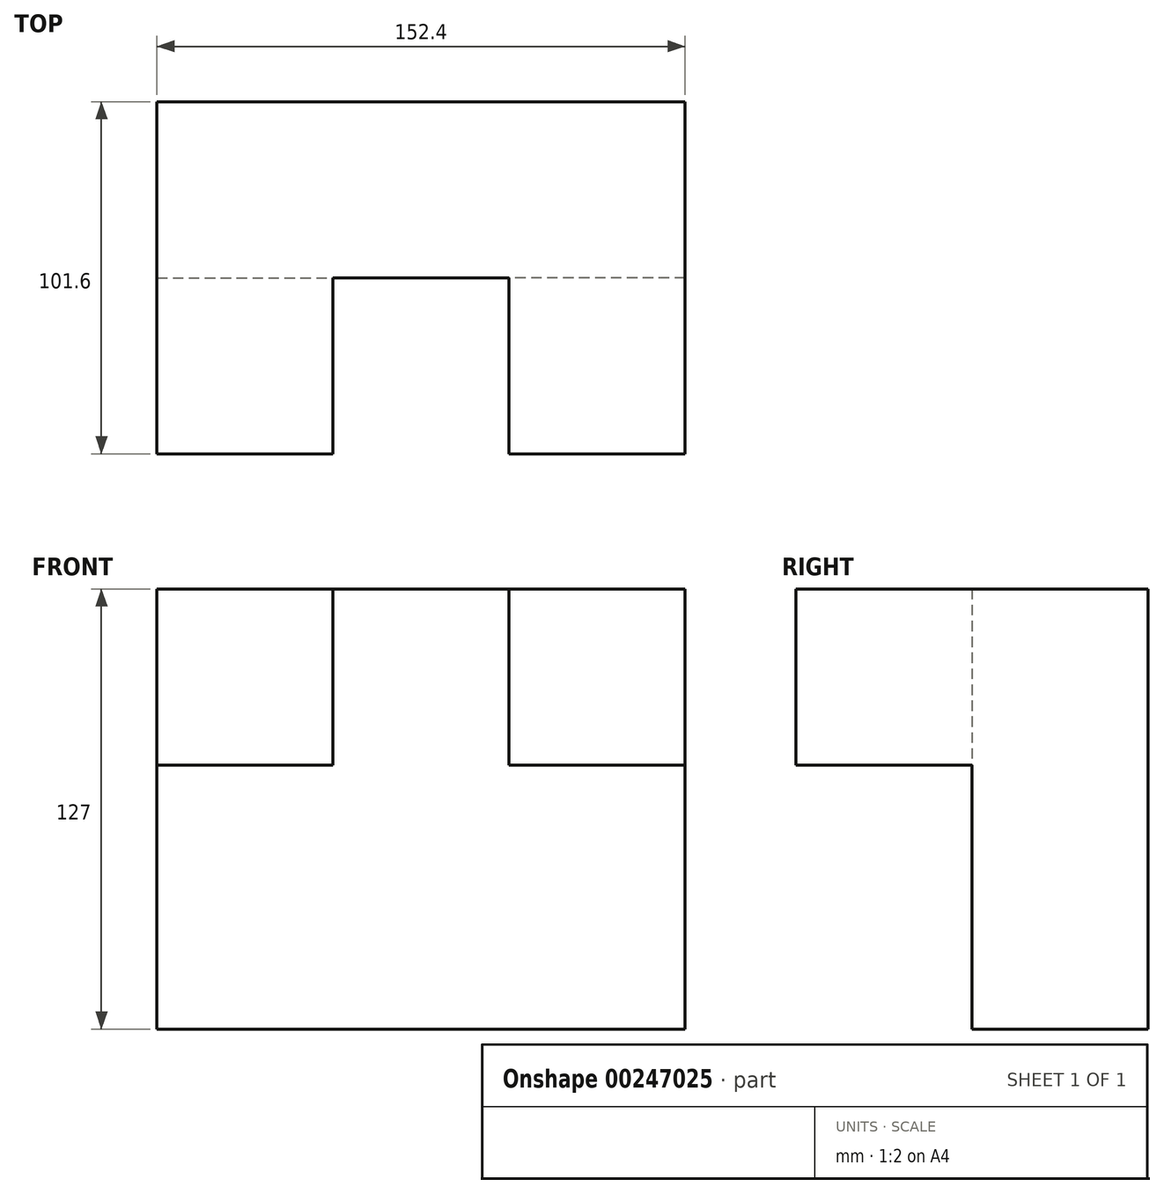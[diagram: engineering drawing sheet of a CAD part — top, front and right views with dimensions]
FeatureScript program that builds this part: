
annotation { "Feature Type Name" : "Feature", "Feature Type Description" : "" }
export const myFeature = defineFeature(function(context is Context, id is Id, definition is map)
    precondition{}
    {
        {
            var Q0;
            Q0=qCreatedBy(makeId("Front.planeOp"),FACE);
            var sketch = newSketch(context, id + "F0", { "sketchPlane" : qUnion([Q0])});
            skLineSegment(sketch, "E0.bottom", {"start": v(-68.04, 132.68) * mm, "end": v(84.36, 132.68) * mm});
            skLineSegment(sketch, "E0.top", {"start": v(-68.04, 5.68) * mm, "end": v(84.36, 5.68) * mm});
            skLineSegment(sketch, "E0.left", {"start": v(-68.04, 132.68) * mm, "end": v(-68.04, 5.68) * mm});
            skLineSegment(sketch, "E0.right", {"start": v(84.36, 132.68) * mm, "end": v(84.36, 5.68) * mm});
            skSolve(sketch);
        }
        {
            var Q0;
            Q0=makeQuery(id+"F0.imprint","IMPRINT",FACE,{"disambiguationData":[TD([[makeQuery(id+"F0.imprint","IMPRINT",EDGE,{"derivedFrom":sQuery(id+"F0.wireOp",EDGE,"E0.bottom")}),-1.0]])]});
            extrude(context, id + "F1", {"entities" : qUnion([Q0]), "depth" : 50.8 * mm});
        }
        {
            var Q0;
            Q0=makeQuery(id+"F1.opExtrude","CAP_FACE",FACE,{"disambiguationData":[OSD([sQuery(id+"F0.wireOp",EDGE,"E0.bottom"),sQuery(id+"F0.wireOp",EDGE,"E0.top"),sQuery(id+"F0.wireOp",EDGE,"E0.left"),sQuery(id+"F0.wireOp",EDGE,"E0.right")])],"isStart":false});
            var sketch = newSketch(context, id + "F2", { "sketchPlane" : qUnion([Q0])});
            skLineSegment(sketch, "E1.bottom", {"start": v(-68.04, 132.68) * mm, "end": v(-17.24, 132.68) * mm});
            skLineSegment(sketch, "E1.top", {"start": v(-68.04, 81.88) * mm, "end": v(-17.24, 81.88) * mm});
            skLineSegment(sketch, "E1.left", {"start": v(-68.04, 132.68) * mm, "end": v(-68.04, 81.88) * mm});
            skLineSegment(sketch, "E1.right", {"start": v(-17.24, 132.68) * mm, "end": v(-17.24, 81.88) * mm});
            skLineSegment(sketch, "E2.bottom", {"start": v(84.36, 132.68) * mm, "end": v(33.56, 132.68) * mm});
            skLineSegment(sketch, "E2.top", {"start": v(84.36, 81.88) * mm, "end": v(33.56, 81.88) * mm});
            skLineSegment(sketch, "E2.left", {"start": v(84.36, 132.68) * mm, "end": v(84.36, 81.88) * mm});
            skLineSegment(sketch, "E2.right", {"start": v(33.56, 132.68) * mm, "end": v(33.56, 81.88) * mm});
            skSolve(sketch);
        }
        {
            var Q0;
            Q0 = qSketchRegion(id + "F2", true);
            extrude(context, id + "F3", {"entities" : qUnion([Q0]), "operationType" : NewBodyOperationType.ADD, "depth" : 50.8 * mm});
        }
    });
